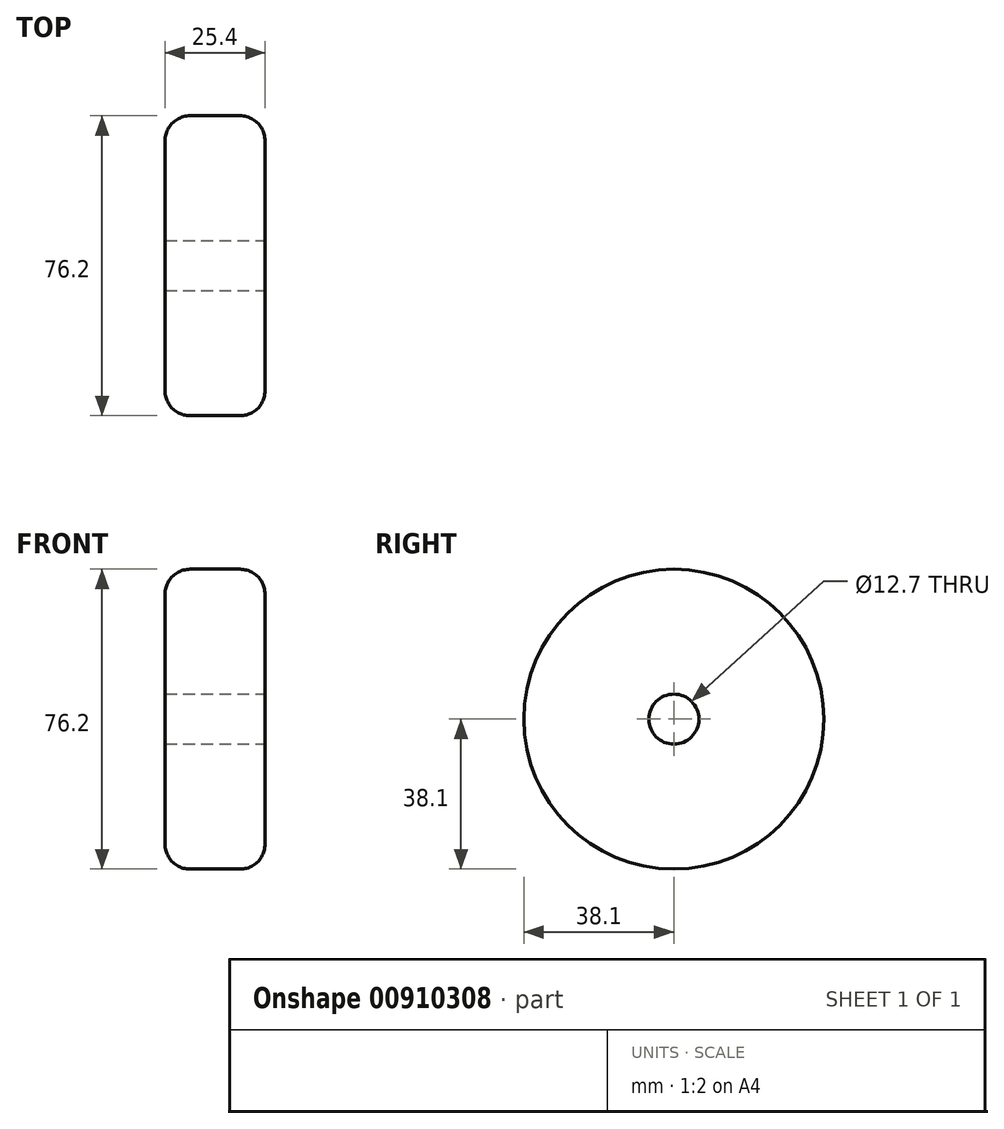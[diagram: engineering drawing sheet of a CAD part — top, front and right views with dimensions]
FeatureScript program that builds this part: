
annotation { "Feature Type Name" : "Feature", "Feature Type Description" : "" }
export const myFeature = defineFeature(function(context is Context, id is Id, definition is map)
    precondition{}
    {
        {
            var Q0;
            Q0=qCreatedBy(makeId("Right.planeOp"),FACE);
            var sketch = newSketch(context, id + "F0", { "sketchPlane" : qUnion([Q0])});
            skCircle(sketch, "E0", {"center": v(0, 0) * mm, "radius": 38.1 * mm});
            skSolve(sketch);
        }
        {
            var Q0;
            Q0 = qSketchRegion(id + "F0", true);
            extrude(context, id + "F1", {"entities" : qUnion([Q0]), "depth" : 25.4 * mm, "offsetDistance" : 25.4 * mm});
        }
        {
            var Q0;
            Q0=makeQuery(id+"F1.opExtrude","CAP_FACE",FACE,{"disambiguationData":[OSD([sQuery(id+"F0.wireOp",EDGE,"E0")])],"isStart":false});
            var sketch = newSketch(context, id + "F2", { "sketchPlane" : qUnion([Q0])});
            skPoint(sketch, "E1", {"position": v(0, 0) * mm});
            skSolve(sketch);
        }
        {
            var Q0;
            Q0=sQuery(id+"F2.wireOp",VERTEX,"E1");
            var Q1;
            Q1=makeQuery(id+"F1.opExtrude","SWEPT_BODY",BODY,{"disambiguationData":[OSD([sQuery(id+"F0.wireOp",EDGE,"E0")])]});
            hole(context, id + "F3", {"style" : HoleStyle.SIMPLE, "endStyle" : HoleEndStyle.THROUGH, "holeDiameter" : 12.7 * mm, "majorDiameter" : 6.35 * mm, "isTappedThrough" : true, "tappedDepth" : 12.7 * mm, "tapClearance" : 3, "locations" : qUnion([Q0]), "scope" : qUnion([Q1])});
        }
        {
            var Q0;
            Q0=makeQuery(id+"F1.opExtrude","CAP_EDGE",EDGE,{"disambiguationData":[OSD([sQuery(id+"F0.wireOp",EDGE,"E0")])],"isStart":false});
            fillet(context, id + "F4", {"entities" : qUnion([Q0]), "radius" : 6.35 * mm, "tangentPropagation" : true, "allowEdgeOverflow" : false});
        }
        {
            var Q0;
            Q0=makeQuery(id+"F1.opExtrude","CAP_EDGE",EDGE,{"disambiguationData":[OSD([sQuery(id+"F0.wireOp",EDGE,"E0")])],"isStart":true});
            fillet(context, id + "F5", {"entities" : qUnion([Q0]), "radius" : 6.35 * mm, "tangentPropagation" : true, "allowEdgeOverflow" : false});
        }
    });
